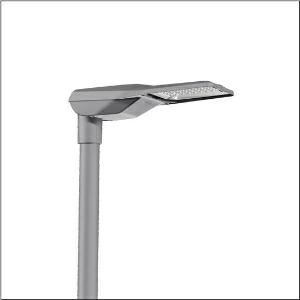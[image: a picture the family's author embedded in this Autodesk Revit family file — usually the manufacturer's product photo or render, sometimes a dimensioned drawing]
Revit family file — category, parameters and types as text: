
# Revit family: streetlight_sl_21_iq_mini___st1_5a_5xe2p31d08gb_fdd6
name_source: partatom
category: Lighting Fixtures
units: mm (PartAtom-declared; Revit-internal decimal feet)

## family parameters
Cut with Voids When Loaded = No
Host = Face
Light Source = No
Part Type = Normal
Room Calculation Point = No
Round Connector Dimension = Use Diameter
Shared = No

## types (1)
- --- (1 x LED, 5580 lm, 37.1 W, 3000K)
    Apparent Load = 37 VA
    CIE Flux Codes = 22 53 95 100 100
    Color Rendering = 70
    Color Temperature = 3000K
    Default Elevation = 1800 mm
    Description = Streetlight SL 21 iQ mini, mast luminaire, primary light control with lens, of PMMA, primary optical cover: cover, of toughened safety glass, transparent, light distribution: ST1.5a, light emission: direct distribution, primary light characteristic: asymmetric, installation type: post-top, side-entry, LED, High Power LED, rated luminous flux: 5.580lm, luminous efficacy: 150lm/W, light colour: 730, colour temperature: 3000K, control: Auto-Match, Temp-Guard, Lumen-Switch, Night-Set, Smart-Wire, Light-Fading, Desk-Remote (wireless, voltage-free reading and setting of iQ features in the workshop via application-optimized NFC function/RFID function), optimised constant luminous flux control (CLO 2.0), presetting dimming linear, mains connection: 220..240V, AC, 50/60Hz, start of lifetime: 37W, end of service life: 39W, reduction: 18W, luminaire housing, of diecast aluminium, powder-coated, Siteco® metallic grey (DB 702S), corrosivity category C5 mid according to DIN EN ISO 12944, please order mast flange separately, inclination adjustable: 0°, 5°, 10°, 15°, sealing non-destructively replaceable, multi-level sealing system, length: 628mm, width: 235mm, height: 110mm, mast flange for spigot size: 42mm (side-entry): 5XC10008XM4, 60/48mm (side-entry/post-top): 5XC10108XM2, 76/60mm (side-entry/post-top): 5XC10108XM1, protection rating (complete): IP66, insulation class (complete): insulation class II (safety insulation), certification: CE, ENEC, ENEC+, VDE, impact resistance: IK09, permissible operating ambient temperature for outdoor applications: -40..+50°C, standard-compliant lighting for roads and squares, packaging unit: 1 piece

Light Distribution: ST1.5a
    Height = 110 mm
    Lamp = 1 x LED
    Lamp Light Flux = 5580 lm
    Lamp Power = 37.1 W
    Lamp count = 1
    Length = 625 mm
    Luminous efficacy = 150 lm/W
    Manufacturer = Siteco
    ModVariant = No
    Model = 5XE2P31D08GB
    Number of Poles = 1
    OnlyDefault = Yes
    Power Factor = 1
    Product Name = Streetlight SL 21 iQ mini | ST1.5a
    Product group = mast luminaire | pylon top
    ProductGroupID = 6100
    Protection Class = Protection class II
    Protection Degree = IP 66
    RLX_Detail_Level = 1
    RLX_Emergency_Light_Flux = 0 lm
    RLX_Emergency_Type = 0
    RLX_Emergency_Type_DB = No
    RlxData = <blob elided: 97061 chars, md5=d56f43b8>
    Socket = socket
    Standby Power = 0 W
    System Light Flux = 5580 lm
    System Power = 37 W
    Type Comments = factory setting: luminous flux: 100 % | dim-lin: 254 | 385 mA
    Type Image = l_1003519.jpg
    URL = http://relux.com
    VarID = @adj_109087
    Voltage = 0 V
    Weight = 0.00 kg
    Width = 234 mm

## geometry (parser evidence)
native form markers: Blend x4, Sweep x11
no freeform markers — native parametric forms only
